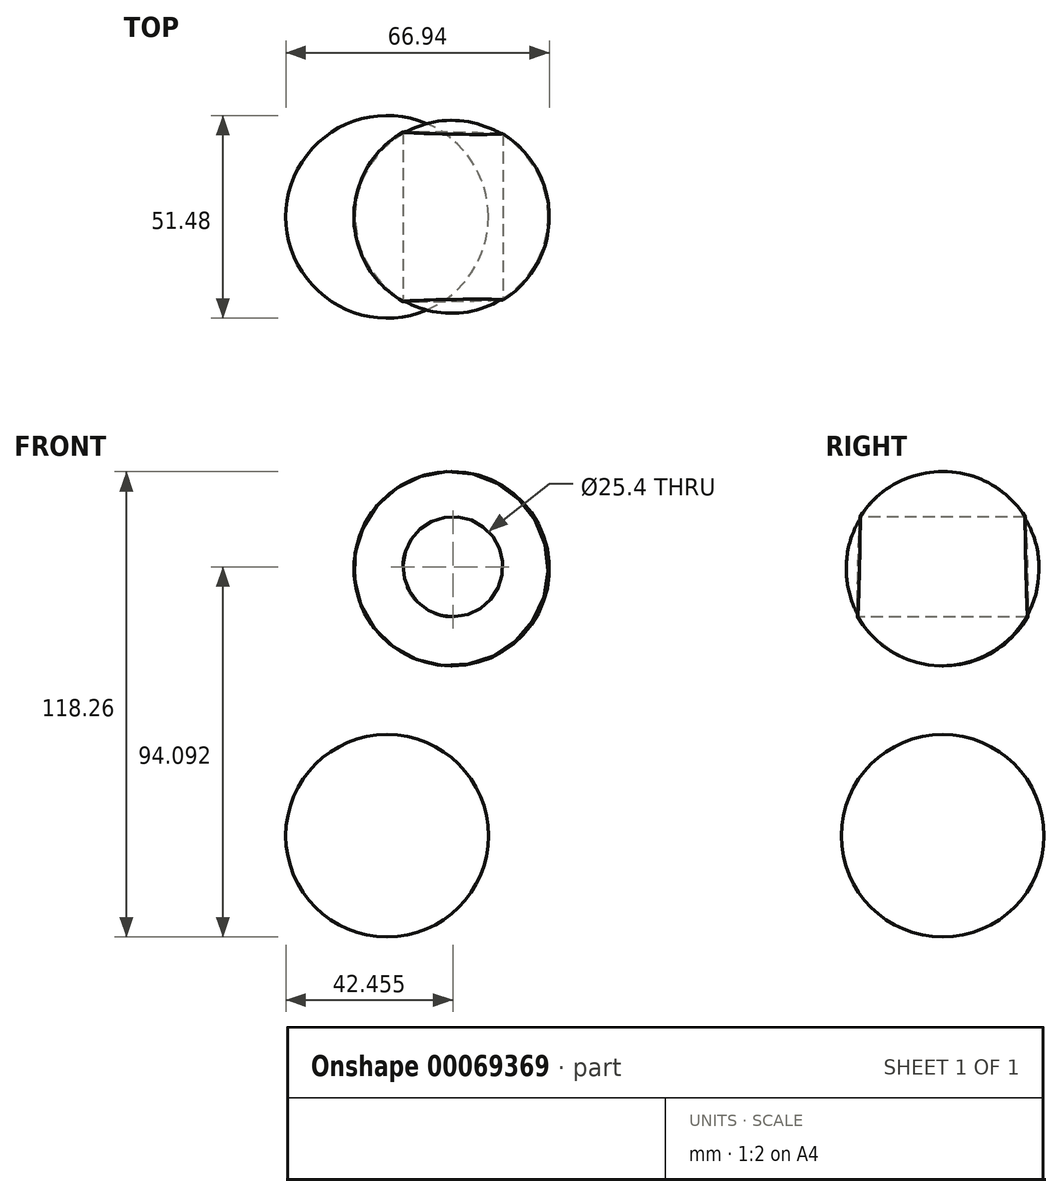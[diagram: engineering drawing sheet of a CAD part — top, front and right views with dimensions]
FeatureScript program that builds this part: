
annotation { "Feature Type Name" : "Feature", "Feature Type Description" : "" }
export const myFeature = defineFeature(function(context is Context, id is Id, definition is map)
    precondition{}
    {
        {
            var Q0;
            Q0=qCreatedBy(makeId("Front.planeOp"),FACE);
            var sketch = newSketch(context, id + "F0", { "sketchPlane" : qUnion([Q0])});
            skLineSegment(sketch, "E0", {"start": v(-38.1, 0) * mm, "end": v(38.1, 0) * mm});
            skLineSegment(sketch, "E1", {"start": v(38.1, 0) * mm, "end": v(0, 38.1) * mm});
            skLineSegment(sketch, "E2", {"start": v(0, 38.1) * mm, "end": v(-38.1, 0) * mm});
            skSolve(sketch);
        }
        {
            var Q0;
            Q0=makeQuery(id+"F0.imprint","IMPRINT",FACE,{"disambiguationData":[TD([[makeQuery(id+"F0.imprint","IMPRINT",EDGE,{"derivedFrom":sQuery(id+"F0.wireOp",EDGE,"E0")}),1.0]])]});
            extrude(context, id + "F1", {"entities" : qUnion([Q0]), "endBound" : BoundingType.SYMMETRIC, "depth" : 31.75 * mm});
        }
        {
            var Q0;
            Q0=makeQuery(id+"F1.opExtrude","SWEPT_FACE",FACE,{"disambiguationData":[OSD([sQuery(id+"F0.wireOp",EDGE,"E2")])]});
            var sketch = newSketch(context, id + "F2", { "sketchPlane" : qUnion([Q0])});
            skLineSegment(sketch, "E3", {"start": v(26.94, 15.88) * mm, "end": v(26.94, -15.88) * mm});
            skLineSegment(sketch, "E4", {"start": v(26.94, -15.88) * mm, "end": v(-26.94, -15.88) * mm});
            skLineSegment(sketch, "E5", {"start": v(-26.94, -15.88) * mm, "end": v(-26.94, 15.88) * mm});
            skLineSegment(sketch, "E6", {"start": v(-26.94, 15.88) * mm, "end": v(26.94, 15.88) * mm});
            skCircle(sketch, "E7", {"center": v(26.94, 15.88) * mm, "radius": 19.05 * mm});
            skSolve(sketch);
        }
        {
            var Q0;
            Q0 = qSketchRegion(id + "F2", true);
            extrude(context, id + "F3", {"entities" : qUnion([Q0]), "operationType" : NewBodyOperationType.ADD, "depth" : 50.8 * mm});
        }
        {
            var Q0;
            Q0=qCreatedBy(makeId("Front.planeOp"),FACE);
            var sketch = newSketch(context, id + "F4", { "sketchPlane" : qUnion([Q0])});
            skLineSegment(sketch, "E8", {"start": v(53.62, 59.1) * mm, "end": v(53.62, 9.78) * mm});
            skArc(sketch, "E9", {"start": v(53.62, 9.78) * mm, "mid": v(78.44, 34.44) * mm, "end": v(53.62, 59.1) * mm});
            skSolve(sketch);
        }
        {
            var Q0;
            Q0=makeQuery(id+"F4.imprint","IMPRINT",FACE,{"disambiguationData":[TD([[makeQuery(id+"F4.imprint","IMPRINT",EDGE,{"derivedFrom":sQuery(id+"F4.wireOp",EDGE,"E8")}),1.0]])]});
            var Q1;
            Q1=sQuery(id+"F4.wireOp",EDGE,"E8");
            revolve(context, id + "F5", {"entities" : qUnion([Q0]), "axis" : qUnion([Q1]), "revolveType" : RevolveType.FULL});
        }
        {
            var Q0;
            Q0=qCreatedBy(makeId("Front.planeOp"),FACE);
            var sketch = newSketch(context, id + "F6", { "sketchPlane" : qUnion([Q0])});
            skLineSegment(sketch, "E10", {"start": v(-58.94, 0) * mm, "end": v(-58.94, -61) * mm});
            skArc(sketch, "E11", {"start": v(-58.94, -61) * mm, "mid": v(-28.12, -30.5) * mm, "end": v(-58.94, 0) * mm});
            skSolve(sketch);
        }
        {
            var Q0;
            Q0=makeQuery(id+"F6.imprint","IMPRINT",FACE,{"disambiguationData":[TD([[makeQuery(id+"F6.imprint","IMPRINT",EDGE,{"derivedFrom":sQuery(id+"F6.wireOp",EDGE,"E10")}),1.0]])]});
            var Q1;
            Q1=sQuery(id+"F6.wireOp",EDGE,"E10");
            revolve(context, id + "F7", {"entities" : qUnion([Q0]), "axis" : qUnion([Q1]), "revolveType" : RevolveType.FULL});
        }
        {
            var Q0;
            Q0=qCreatedBy(makeId("Front.planeOp"),FACE);
            var sketch = newSketch(context, id + "F8", { "sketchPlane" : qUnion([Q0])});
            skLineSegment(sketch, "E12", {"start": v(37.23, -7.68) * mm, "end": v(37.23, -59.15) * mm});
            skArc(sketch, "E13", {"start": v(37.23, -59.15) * mm, "mid": v(62.97, -33.42) * mm, "end": v(37.23, -7.68) * mm});
            skSolve(sketch);
        }
        {
            var Q0;
            Q0=makeQuery(id+"F8.imprint","IMPRINT",FACE,{"disambiguationData":[TD([[makeQuery(id+"F8.imprint","IMPRINT",EDGE,{"derivedFrom":sQuery(id+"F8.wireOp",EDGE,"E12")}),1.0]])]});
            var Q1;
            Q1=sQuery(id+"F8.wireOp",EDGE,"E12");
            revolve(context, id + "F9", {"entities" : qUnion([Q0]), "axis" : qUnion([Q1]), "revolveType" : RevolveType.FULL});
        }
        {
            var Q0;
            Q0=makeQuery(id+"F1.opExtrude","SWEPT_BODY",BODY,{"disambiguationData":[OSD([sQuery(id+"F0.wireOp",EDGE,"E0"),sQuery(id+"F0.wireOp",EDGE,"E1"),sQuery(id+"F0.wireOp",EDGE,"E2")])]});
            deleteBodies(context, id + "F10", {"entities" : qUnion([Q0])});
        }
        {
            var Q0;
            Q0=qCreatedBy(makeId("Front.planeOp"),FACE);
            var sketch = newSketch(context, id + "F11", { "sketchPlane" : qUnion([Q0])});
            skCircle(sketch, "E14", {"center": v(53.95, 34.94) * mm, "radius": 12.7 * mm});
            skSolve(sketch);
        }
        {
            var Q0;
            Q0 = qSketchRegion(id + "F11", true);
            extrude(context, id + "F12", {"entities" : qUnion([Q0]), "operationType" : NewBodyOperationType.REMOVE, "endBound" : BoundingType.SYMMETRIC, "oppositeDirection" : true, "depth" : 50.8 * mm});
        }
        {
            var Q0;
            Q0=makeQuery(id+"F7.opRevolve","SWEPT_BODY",BODY,{"disambiguationData":[OSD([sQuery(id+"F6.wireOp",EDGE,"E10"),sQuery(id+"F6.wireOp",EDGE,"E11")])]});
            deleteBodies(context, id + "F13", {"entities" : qUnion([Q0])});
        }
    });
